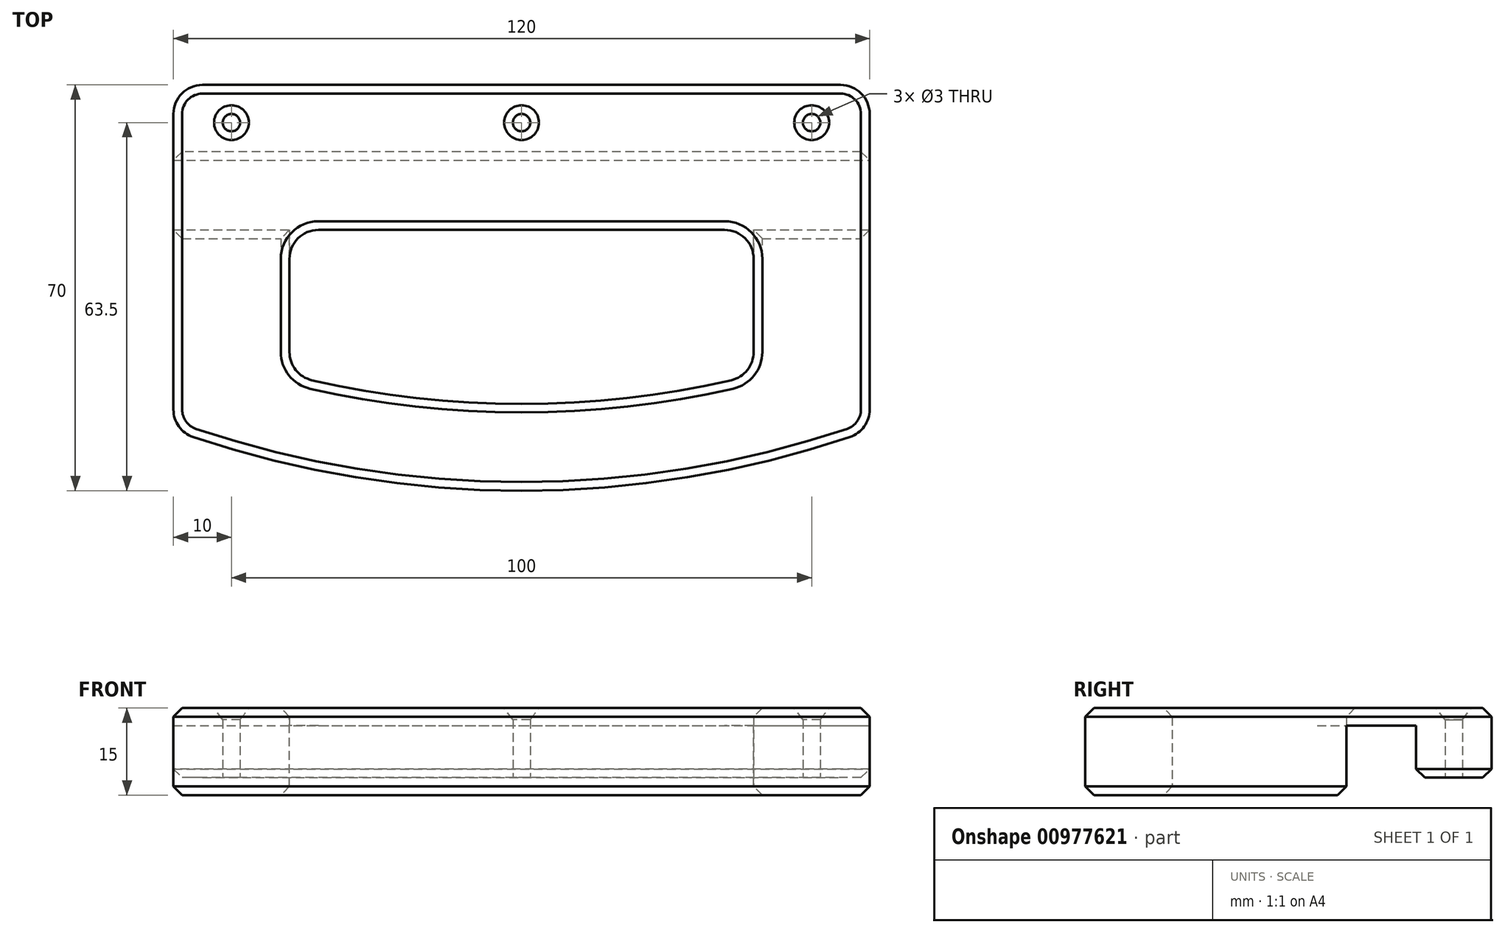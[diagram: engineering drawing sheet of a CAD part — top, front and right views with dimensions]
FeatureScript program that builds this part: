
annotation { "Feature Type Name" : "Feature", "Feature Type Description" : "" }
export const myFeature = defineFeature(function(context is Context, id is Id, definition is map)
    precondition{}
    {
        {
            var Q0;
            Q0=qCreatedBy(makeId("Top.planeOp"),FACE);
            var sketch = newSketch(context, id + "F0", { "sketchPlane" : qUnion([Q0])});
            skLineSegment(sketch, "E0", {"start": v(0, 0) * mm, "end": v(80, 0) * mm});
            skLineSegment(sketch, "E1", {"start": v(80, 0) * mm, "end": v(80, -25) * mm});
            skLineSegment(sketch, "E2", {"start": v(0, 0) * mm, "end": v(0, -25) * mm});
            skArc(sketch, "E3", {"start": v(0, -25) * mm, "mid": v(40, -30) * mm, "end": v(80, -25) * mm});
            skArc(sketch, "E4.0", {"start": v(-20, -34.55) * mm, "mid": v(40, -45) * mm, "end": v(100, -34.55) * mm});
            skLineSegment(sketch, "E5.0", {"start": v(-20, 25) * mm, "end": v(-20, -34.55) * mm});
            skLineSegment(sketch, "E6.0", {"start": v(100, 25) * mm, "end": v(100, -34.55) * mm});
            skLineSegment(sketch, "E7.0", {"start": v(-20, 25) * mm, "end": v(100, 25) * mm});
            skLineSegment(sketch, "E8", {"start": v(-20, 12) * mm, "end": v(100, 12) * mm});
            skLineSegment(sketch, "E9", {"start": v(-20, 0) * mm, "end": v(0, 0) * mm});
            skLineSegment(sketch, "E10", {"start": v(80, 0) * mm, "end": v(100, 0) * mm});
            skLineSegment(sketch, "E11", {"start": v(-20, 18.5) * mm, "end": v(100, 18.5) * mm, "construction": true});
            skCircle(sketch, "E12", {"center": v(40, 18.5) * mm, "radius": 1.5 * mm});
            skCircle(sketch, "E13", {"center": v(90, 18.5) * mm, "radius": 1.5 * mm});
            skCircle(sketch, "E14", {"center": v(-10, 18.5) * mm, "radius": 1.5 * mm});
            skSolve(sketch);
        }
        {
            var Q0;
            {var subQ0=sQuery(id+"F0.wireOp",EDGE,"E7.0");Q0=makeQuery(id+"F0.imprint","IMPRINT",FACE,{"disambiguationData":[TD([[makeQuery(id+"F0.imprint","IMPRINT",EDGE,{"derivedFrom":subQ0}),-1.0]])]});}
            var Q1;
            Q1=makeQuery(id+"F0.imprint","IMPRINT",FACE,{"disambiguationData":[TD([[makeQuery(id+"F0.imprint","IMPRINT",EDGE,{"derivedFrom":sQuery(id+"F0.wireOp",EDGE,"E0")}),1.0]])]});
            var Q2;
            Q2=makeQuery(id+"F0.imprint","IMPRINT",FACE,{"disambiguationData":[TD([[makeQuery(id+"F0.imprint","IMPRINT",EDGE,{"derivedFrom":sQuery(id+"F0.wireOp",EDGE,"E1")}),1.0]])]});
            extrude(context, id + "F1", {"entities" : qUnion([Q0, Q1, Q2]), "depth" : 3 * mm, "offsetDistance" : 25 * mm});
        }
        {
            var Q0;
            {var subQ0=sQuery(id+"F0.wireOp",EDGE,"E7.0");Q0=makeQuery(id+"F0.imprint","IMPRINT",FACE,{"disambiguationData":[TD([[makeQuery(id+"F0.imprint","IMPRINT",EDGE,{"derivedFrom":subQ0}),-1.0]])]});}
            extrude(context, id + "F2", {"entities" : qUnion([Q0]), "operationType" : NewBodyOperationType.ADD, "oppositeDirection" : true, "depth" : 9 * mm, "offsetDistance" : 25 * mm});
        }
        {
            var Q0;
            Q0=makeQuery(id+"F0.imprint","IMPRINT",FACE,{"disambiguationData":[TD([[makeQuery(id+"F0.imprint","IMPRINT",EDGE,{"derivedFrom":sQuery(id+"F0.wireOp",EDGE,"E1")}),1.0]])]});
            extrude(context, id + "F3", {"entities" : qUnion([Q0]), "operationType" : NewBodyOperationType.ADD, "oppositeDirection" : true, "depth" : 12 * mm, "offsetDistance" : 25 * mm});
        }
        {
            var Q0;
            {var subQ0=sQuery(id+"F0.wireOp",EDGE,"E5.0");var subQ1=sQuery(id+"F0.wireOp",EDGE,"E4.0");Q0=makeQuery(id+"F3.boolean.opBoolean","MERGE",EDGE,{"derivedFrom":[makeQuery(id+"F1.opExtrude","SWEPT_EDGE",EDGE,{"disambiguationData":[OSD([subQ1,subQ0])]}),makeQuery(id+"F3.opExtrude","SWEPT_EDGE",EDGE,{"disambiguationData":[OSD([subQ1,subQ0])]})]});}
            var Q1;
            {var subQ0=sQuery(id+"F0.wireOp",EDGE,"E6.0");var subQ1=sQuery(id+"F0.wireOp",EDGE,"E4.0");Q1=makeQuery(id+"F3.boolean.opBoolean","MERGE",EDGE,{"derivedFrom":[makeQuery(id+"F1.opExtrude","SWEPT_EDGE",EDGE,{"disambiguationData":[OSD([subQ1,subQ0])]}),makeQuery(id+"F3.opExtrude","SWEPT_EDGE",EDGE,{"disambiguationData":[OSD([subQ1,subQ0])]})]});}
            var Q2;
            Q2=makeQuery(id+"F1.opExtrude","SWEPT_EDGE",EDGE,{"disambiguationData":[OSD([sQuery(id+"F0.wireOp",EDGE,"E0"),sQuery(id+"F0.wireOp",EDGE,"E2"),sQuery(id+"F0.wireOp",EDGE,"E9")])]});
            var Q3;
            Q3=makeQuery(id+"F1.opExtrude","SWEPT_EDGE",EDGE,{"disambiguationData":[OSD([sQuery(id+"F0.wireOp",EDGE,"E0"),sQuery(id+"F0.wireOp",EDGE,"E1"),sQuery(id+"F0.wireOp",EDGE,"E10")])]});
            var Q4;
            {var subQ0=sQuery(id+"F0.wireOp",EDGE,"E3");var subQ1=sQuery(id+"F0.wireOp",EDGE,"E1");Q4=makeQuery(id+"F3.boolean.opBoolean","MERGE",EDGE,{"derivedFrom":[makeQuery(id+"F1.opExtrude","SWEPT_EDGE",EDGE,{"disambiguationData":[OSD([subQ1,subQ0])]}),makeQuery(id+"F3.opExtrude","SWEPT_EDGE",EDGE,{"disambiguationData":[OSD([subQ1,subQ0])]})]});}
            var Q5;
            {var subQ0=sQuery(id+"F0.wireOp",EDGE,"E3");var subQ1=sQuery(id+"F0.wireOp",EDGE,"E2");Q5=makeQuery(id+"F3.boolean.opBoolean","MERGE",EDGE,{"derivedFrom":[makeQuery(id+"F1.opExtrude","SWEPT_EDGE",EDGE,{"disambiguationData":[OSD([subQ1,subQ0])]}),makeQuery(id+"F3.opExtrude","SWEPT_EDGE",EDGE,{"disambiguationData":[OSD([subQ1,subQ0])]})]});}
            var Q6;
            {var subQ0=sQuery(id+"F0.wireOp",EDGE,"E7.0");var subQ1=sQuery(id+"F0.wireOp",EDGE,"E6.0");Q6=makeQuery(id+"F2.boolean.opBoolean","MERGE",EDGE,{"derivedFrom":[makeQuery(id+"F1.opExtrude","SWEPT_EDGE",EDGE,{"disambiguationData":[OSD([subQ1,subQ0])]}),makeQuery(id+"F2.opExtrude","SWEPT_EDGE",EDGE,{"disambiguationData":[OSD([subQ1,subQ0])]})]});}
            var Q7;
            {var subQ0=sQuery(id+"F0.wireOp",EDGE,"E7.0");var subQ1=sQuery(id+"F0.wireOp",EDGE,"E5.0");Q7=makeQuery(id+"F2.boolean.opBoolean","MERGE",EDGE,{"derivedFrom":[makeQuery(id+"F1.opExtrude","SWEPT_EDGE",EDGE,{"disambiguationData":[OSD([subQ1,subQ0])]}),makeQuery(id+"F2.opExtrude","SWEPT_EDGE",EDGE,{"disambiguationData":[OSD([subQ1,subQ0])]})]});}
            fillet(context, id + "F4", {"entities" : qUnion([Q0, Q1, Q2, Q3, Q4, Q5, Q6, Q7]), "radius" : 5 * mm, "tangentPropagation" : true, "allowEdgeOverflow" : false});
        }
        {
            var Q0;
            Q0=makeQuery(id+"F1.opExtrude","CAP_EDGE",EDGE,{"disambiguationData":[OSD([sQuery(id+"F0.wireOp",EDGE,"E14")])],"isStart":false});
            var Q1;
            Q1=makeQuery(id+"F1.opExtrude","CAP_EDGE",EDGE,{"disambiguationData":[OSD([sQuery(id+"F0.wireOp",EDGE,"E12")])],"isStart":false});
            var Q2;
            Q2=makeQuery(id+"F1.opExtrude","CAP_EDGE",EDGE,{"disambiguationData":[OSD([sQuery(id+"F0.wireOp",EDGE,"E13")])],"isStart":false});
            chamfer(context, id + "F5", {"entities" : qUnion([Q0, Q1, Q2]), "chamferType" : ChamferType.TWO_OFFSETS, "width1" : 2 * mm, "oppositeDirection" : false, "width2" : 1.5 * mm, "tangentPropagation" : true});
        }
        {
            var Q0;
            Q0=makeQuery(id+"F1.opExtrude","CAP_EDGE",EDGE,{"disambiguationData":[OSD([sQuery(id+"F0.wireOp",EDGE,"E0")])],"isStart":false});
            var Q1;
            Q1=makeQuery(id+"F1.opExtrude","CAP_EDGE",EDGE,{"disambiguationData":[OSD([sQuery(id+"F0.wireOp",EDGE,"E5.0")])],"isStart":false});
            var Q2;
            Q2=makeQuery(id+"F3.opExtrude","CAP_FACE",FACE,{"disambiguationData":[OSD([sQuery(id+"F0.wireOp",EDGE,"E1"),sQuery(id+"F0.wireOp",EDGE,"E2"),sQuery(id+"F0.wireOp",EDGE,"E3"),sQuery(id+"F0.wireOp",EDGE,"E4.0"),sQuery(id+"F0.wireOp",EDGE,"E5.0"),sQuery(id+"F0.wireOp",EDGE,"E6.0"),sQuery(id+"F0.wireOp",EDGE,"E9"),sQuery(id+"F0.wireOp",EDGE,"E10")])],"isStart":false});
            var Q3;
            Q3=makeQuery(id+"F2.opExtrude","CAP_EDGE",EDGE,{"disambiguationData":[OSD([sQuery(id+"F0.wireOp",EDGE,"E8")])],"isStart":false});
            var Q4;
            Q4=makeQuery(id+"F2.opExtrude","CAP_EDGE",EDGE,{"disambiguationData":[OSD([sQuery(id+"F0.wireOp",EDGE,"E7.0")])],"isStart":false});
            chamfer(context, id + "F6", {"entities" : qUnion([Q0, Q1, Q2, Q3, Q4]), "width" : 1.5 * mm, "tangentPropagation" : true});
        }
    });
